# Revit family: SolarStone_Roof_Panels_Benders_90W2
name_source: partatom
category: Electrical Fixtures
revit_build: Autodesk Revit 2018 (Build: 20170223_1515(x64)
units: mm (PartAtom-declared; Revit-internal decimal feet)

## family parameters
Always vertical = No
Cut with Voids When Loaded = No
Host = Roof
Maintain Annotation Orientation = No
Part Type = Normal
Room Calculation Point = No
Round Connector Dimension = Use Diameter
Shared = No

## types (1)
- SolarStone 90W Module
    Cell type = Monocrystalline, 156 x 156 mm
    Certifications = IEC 61215
    Developer = TULITEC
    Dimensions (mm) = 1530 x 395 x 21
    Dimensions (mm, installed) = 1492 x 331... 370 x 21
    Fire Rating = Class C
    Fixing Plate = SolarStone® - Fixing Plate
    Fuse Rating = 12 A
    Manufacturer = SolarStone
    Maximum Power Current (Imp) = 9 A
    Maximum Power Rating (Pmax) = 90 VA
    Maximum Power Voltage (Vmp) = 12 V
    Maximum System Voltage = 1000 V
    Model Name = S85B2
    Module Efficiency (%) = 18.5
    Mono Perc Solar Cells = SolarStone® - Mono Perc Solar Cell
    Number of cells = 18
    Open Circuit Voltage (Voc) = 11 V
    Output Terminal = MC4
    Power Temperature Coefficient = -0.414 %/°C
    Prismatic Solar Glass = SolarStone® - Prismatic Solar Glass
    Short Circuit Current (Isc) = 10 A
    SolarStone® Aluminium Framing = SolarStone® - Aluminium, Painted
    Static Load Test Passed = 250.00 kg/m²
    Tolerance of Maximum Power Rating = +3/-3%
    URL = https://solarstone.ee
    Weight (kg) = 8

## geometry (parser evidence)
native form markers: Blend x2, Sweep x8
no freeform markers — native parametric forms only
